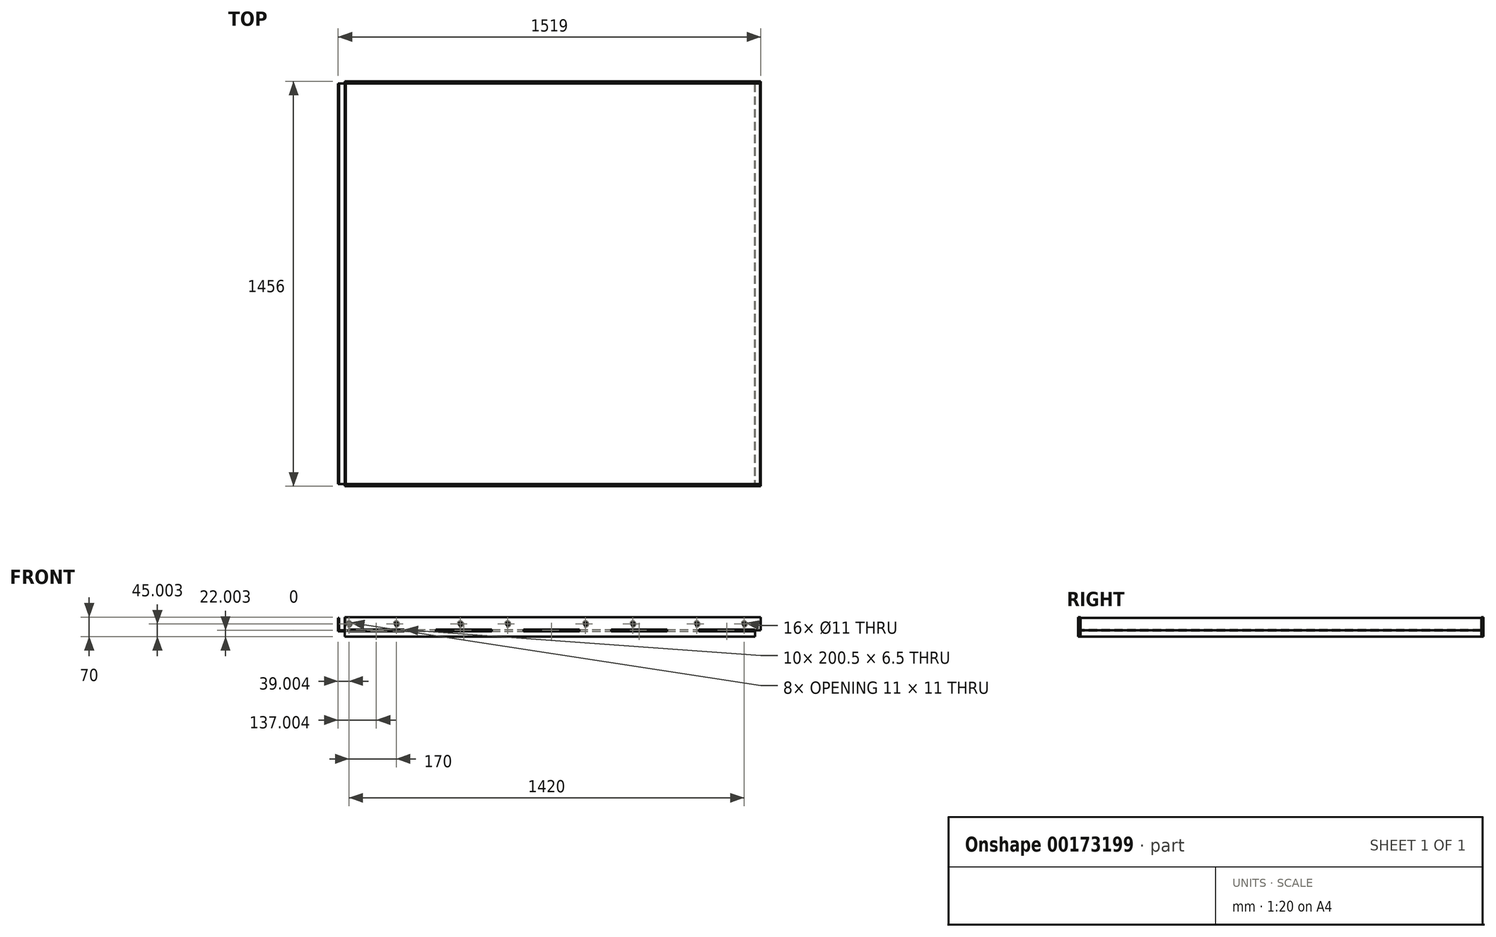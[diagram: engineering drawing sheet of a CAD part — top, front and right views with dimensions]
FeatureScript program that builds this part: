
annotation { "Feature Type Name" : "Feature", "Feature Type Description" : "" }
export const myFeature = defineFeature(function(context is Context, id is Id, definition is map)
    precondition{}
    {
        {
            var Q0;
            Q0=qCreatedBy(makeId("Front.planeOp"),FACE);
            var sketch = newSketch(context, id + "F0", { "sketchPlane" : qUnion([Q0])});
            skLineSegment(sketch, "E0", {"start": v(-1403.49, 88.26) * mm, "end": v(-1403.49, 40.26) * mm});
            skLineSegment(sketch, "E1", {"start": v(-1403.49, 40.26) * mm, "end": v(91.51, 40.26) * mm});
            skLineSegment(sketch, "E2", {"start": v(91.51, 40.26) * mm, "end": v(91.51, 21.26) * mm});
            skLineSegment(sketch, "E3", {"start": v(91.51, 21.26) * mm, "end": v(94.51, 21.26) * mm});
            skLineSegment(sketch, "E4", {"start": v(94.51, 21.26) * mm, "end": v(94.51, 43.26) * mm});
            skLineSegment(sketch, "E5", {"start": v(94.51, 43.26) * mm, "end": v(-1400.49, 43.26) * mm});
            skLineSegment(sketch, "E6", {"start": v(-1400.49, 43.26) * mm, "end": v(-1400.49, 88.26) * mm});
            skLineSegment(sketch, "E7", {"start": v(-1400.49, 88.26) * mm, "end": v(-1403.49, 88.26) * mm});
            skLineSegment(sketch, "E8", {"start": v(-1379.49, 43.26) * mm, "end": v(-1379.49, 88.26) * mm});
            skLineSegment(sketch, "E9", {"start": v(-1379.49, 88.26) * mm, "end": v(-1376.49, 88.26) * mm});
            skLineSegment(sketch, "E10", {"start": v(-1376.49, 88.26) * mm, "end": v(-1376.49, 46.26) * mm});
            skLineSegment(sketch, "E11", {"start": v(-1376.49, 46.26) * mm, "end": v(112.51, 46.26) * mm});
            skLineSegment(sketch, "E12", {"start": v(115.51, 46.26) * mm, "end": v(115.51, 43.26) * mm});
            skLineSegment(sketch, "E13", {"start": v(-1379.49, 43.26) * mm, "end": v(115.51, 43.26) * mm});
            skLineSegment(sketch, "E14", {"start": v(115.51, 46.26) * mm, "end": v(115.51, 88.26) * mm});
            skLineSegment(sketch, "E15", {"start": v(115.51, 88.26) * mm, "end": v(112.51, 88.26) * mm});
            skLineSegment(sketch, "E16", {"start": v(112.51, 88.26) * mm, "end": v(112.51, 46.26) * mm});
            skLineSegment(sketch, "E17.bottom", {"start": v(-1397.49, 82.67) * mm, "end": v(-1382.49, 82.67) * mm, "construction": true});
            skLineSegment(sketch, "E17.top", {"start": v(-1397.49, 47.75) * mm, "end": v(-1382.49, 47.75) * mm, "construction": true});
            skLineSegment(sketch, "E17.left", {"start": v(-1397.49, 82.67) * mm, "end": v(-1397.49, 47.75) * mm, "construction": true});
            skLineSegment(sketch, "E17.right", {"start": v(-1382.49, 82.67) * mm, "end": v(-1382.49, 47.75) * mm, "construction": true});
            skSolve(sketch);
        }
        {
            var Q0;
            Q0=makeQuery(id+"F0.imprint","IMPRINT",FACE,{"disambiguationData":[TD([[makeQuery(id+"F0.imprint","IMPRINT",EDGE,{"derivedFrom":sQuery(id+"F0.wireOp",EDGE,"E0")}),1.0]])]});
            extrude(context, id + "F1", {"entities" : qUnion([Q0]), "oppositeDirection" : true, "depth" : 1440 * mm});
        }
        {
            var Q0;
            {var subQ0=sQuery(id+"F0.wireOp",EDGE,"E8");Q0=makeQuery(id+"F0.imprint","IMPRINT",FACE,{"disambiguationData":[TD([[makeQuery(id+"F0.imprint","IMPRINT",EDGE,{"derivedFrom":subQ0}),-1.0]])]});}
            extrude(context, id + "F2", {"entities" : qUnion([Q0]), "oppositeDirection" : true, "depth" : 1440 * mm});
        }
        {
            var Q0;
            Q0=makeQuery(id+"F1.opExtrude","SWEPT_FACE",FACE,{"disambiguationData":[OSD([sQuery(id+"F0.wireOp",EDGE,"E5"),sQuery(id+"F0.wireOp",EDGE,"E13")])]});
            var sketch = newSketch(context, id + "F3", { "sketchPlane" : qUnion([Q0])});
            skLineSegment(sketch, "E18.bottom", {"start": v(-1366.49, 0) * mm, "end": v(-1166.49, 0) * mm});
            skLineSegment(sketch, "E18.top", {"start": v(-1366.49, -7) * mm, "end": v(-1166.49, -7) * mm});
            skLineSegment(sketch, "E18.left", {"start": v(-1366.49, 0) * mm, "end": v(-1366.49, -7) * mm});
            skLineSegment(sketch, "E18.right", {"start": v(-1166.49, 0) * mm, "end": v(-1166.49, -7) * mm});
            skLineSegment(sketch, "E19.1.0.0", {"start": v(-1051.49, 0) * mm, "end": v(-851.49, 0) * mm});
            skLineSegment(sketch, "E19.1.0.1", {"start": v(-1051.49, -7) * mm, "end": v(-851.49, -7) * mm});
            skLineSegment(sketch, "E19.1.0.2", {"start": v(-851.49, 0) * mm, "end": v(-851.49, -7) * mm});
            skLineSegment(sketch, "E19.1.0.3", {"start": v(-1051.49, 0) * mm, "end": v(-1051.49, -7) * mm});
            skLineSegment(sketch, "E19.2.0.0", {"start": v(-736.49, 0) * mm, "end": v(-536.49, 0) * mm});
            skLineSegment(sketch, "E19.2.0.1", {"start": v(-736.49, -7) * mm, "end": v(-536.49, -7) * mm});
            skLineSegment(sketch, "E19.2.0.2", {"start": v(-536.49, 0) * mm, "end": v(-536.49, -7) * mm});
            skLineSegment(sketch, "E19.2.0.3", {"start": v(-736.49, 0) * mm, "end": v(-736.49, -7) * mm});
            skLineSegment(sketch, "E19.3.0.0", {"start": v(-421.49, 0) * mm, "end": v(-221.49, 0) * mm});
            skLineSegment(sketch, "E19.3.0.1", {"start": v(-421.49, -7) * mm, "end": v(-221.49, -7) * mm});
            skLineSegment(sketch, "E19.3.0.2", {"start": v(-221.49, 0) * mm, "end": v(-221.49, -7) * mm});
            skLineSegment(sketch, "E19.3.0.3", {"start": v(-421.49, 0) * mm, "end": v(-421.49, -7) * mm});
            skLineSegment(sketch, "E19.4.0.0", {"start": v(-106.49, 0) * mm, "end": v(93.51, 0) * mm});
            skLineSegment(sketch, "E19.4.0.1", {"start": v(-106.49, -7) * mm, "end": v(93.51, -7) * mm});
            skLineSegment(sketch, "E19.4.0.2", {"start": v(93.51, 0) * mm, "end": v(93.51, -7) * mm});
            skLineSegment(sketch, "E19.4.0.3", {"start": v(-106.49, 0) * mm, "end": v(-106.49, -7) * mm});
            skLineSegment(sketch, "E19.direction1", {"start": v(-1366.49, -7) * mm, "end": v(-1051.49, -7) * mm, "construction": true});
            skLineSegment(sketch, "E20", {"start": v(-1400.49, 720) * mm, "end": v(412.72, 720) * mm, "construction": true});
            skLineSegment(sketch, "E21.MirrorCS", {"start": v(-1366.49, 1440) * mm, "end": v(-1366.49, 1447) * mm});
            skLineSegment(sketch, "E22.MirrorCS", {"start": v(-1051.49, 1440) * mm, "end": v(-1051.49, 1447) * mm});
            skLineSegment(sketch, "E23.MirrorCS", {"start": v(-421.49, 1440) * mm, "end": v(-421.49, 1447) * mm});
            skLineSegment(sketch, "E24.MirrorCS", {"start": v(93.51, 1440) * mm, "end": v(93.51, 1447) * mm});
            skLineSegment(sketch, "E25.MirrorCS", {"start": v(-221.49, 1440) * mm, "end": v(-221.49, 1447) * mm});
            skLineSegment(sketch, "E26.MirrorCS", {"start": v(-106.49, 1440) * mm, "end": v(-106.49, 1447) * mm});
            skLineSegment(sketch, "E27.MirrorCS", {"start": v(-736.49, 1440) * mm, "end": v(-736.49, 1447) * mm});
            skLineSegment(sketch, "E28.MirrorCS", {"start": v(-536.49, 1440) * mm, "end": v(-536.49, 1447) * mm});
            skLineSegment(sketch, "E29.MirrorCS", {"start": v(-851.49, 1440) * mm, "end": v(-851.49, 1447) * mm});
            skLineSegment(sketch, "E30.MirrorCS", {"start": v(-1166.49, 1440) * mm, "end": v(-1166.49, 1447) * mm});
            skLineSegment(sketch, "E31.MirrorCS", {"start": v(-1366.49, 1440) * mm, "end": v(-1166.49, 1440) * mm});
            skLineSegment(sketch, "E32.MirrorCS", {"start": v(-106.49, 1447) * mm, "end": v(93.51, 1447) * mm});
            skLineSegment(sketch, "E33.MirrorCS", {"start": v(-421.49, 1440) * mm, "end": v(-221.49, 1440) * mm});
            skLineSegment(sketch, "E34.MirrorCS", {"start": v(-736.49, 1440) * mm, "end": v(-536.49, 1440) * mm});
            skLineSegment(sketch, "E35.MirrorCS", {"start": v(-1366.49, 1447) * mm, "end": v(-1166.49, 1447) * mm});
            skLineSegment(sketch, "E36.MirrorCS", {"start": v(-1051.49, 1440) * mm, "end": v(-851.49, 1440) * mm});
            skLineSegment(sketch, "E37.MirrorCS", {"start": v(-106.49, 1440) * mm, "end": v(93.51, 1440) * mm});
            skLineSegment(sketch, "E38.MirrorCS", {"start": v(-421.49, 1447) * mm, "end": v(-221.49, 1447) * mm});
            skLineSegment(sketch, "E39.MirrorCS", {"start": v(-1366.49, 1447) * mm, "end": v(-1051.49, 1447) * mm, "construction": true});
            skLineSegment(sketch, "E40.MirrorCS", {"start": v(-736.49, 1447) * mm, "end": v(-536.49, 1447) * mm});
            skLineSegment(sketch, "E41.MirrorCS", {"start": v(-1051.49, 1447) * mm, "end": v(-851.49, 1447) * mm});
            skSolve(sketch);
        }
        {
            var Q0;
            Q0 = qSketchRegion(id + "F3", true);
            extrude(context, id + "F4", {"entities" : qUnion([Q0]), "operationType" : NewBodyOperationType.ADD, "oppositeDirection" : true, "depth" : 3 * mm});
        }
        {
            var Q0;
            Q0=makeQuery(id+"F2.opExtrude","SWEPT_FACE",FACE,{"disambiguationData":[OSD([sQuery(id+"F0.wireOp",EDGE,"E11")])]});
            var sketch = newSketch(context, id + "F5", { "sketchPlane" : qUnion([Q0])});
            skLineSegment(sketch, "E42.bottom", {"start": v(-1366.49, 0) * mm, "end": v(-1166.49, 0) * mm});
            skLineSegment(sketch, "E42.top", {"start": v(-1366.49, -7) * mm, "end": v(-1166.49, -7) * mm});
            skLineSegment(sketch, "E42.left", {"start": v(-1366.49, 0) * mm, "end": v(-1366.49, -7) * mm});
            skLineSegment(sketch, "E42.right", {"start": v(-1166.49, 0) * mm, "end": v(-1166.49, -7) * mm});
            skLineSegment(sketch, "E43.1.0.0", {"start": v(-1051.49, -7) * mm, "end": v(-851.49, -7) * mm});
            skLineSegment(sketch, "E43.1.0.1", {"start": v(-1051.49, 0) * mm, "end": v(-851.49, 0) * mm});
            skLineSegment(sketch, "E43.1.0.2", {"start": v(-1051.49, 0) * mm, "end": v(-1051.49, -7) * mm});
            skLineSegment(sketch, "E43.1.0.3", {"start": v(-851.49, 0) * mm, "end": v(-851.49, -7) * mm});
            skLineSegment(sketch, "E43.2.0.0", {"start": v(-736.49, -7) * mm, "end": v(-536.49, -7) * mm});
            skLineSegment(sketch, "E43.2.0.1", {"start": v(-736.49, 0) * mm, "end": v(-536.49, 0) * mm});
            skLineSegment(sketch, "E43.2.0.2", {"start": v(-736.49, 0) * mm, "end": v(-736.49, -7) * mm});
            skLineSegment(sketch, "E43.2.0.3", {"start": v(-536.49, 0) * mm, "end": v(-536.49, -7) * mm});
            skLineSegment(sketch, "E43.3.0.0", {"start": v(-421.49, -7) * mm, "end": v(-221.49, -7) * mm});
            skLineSegment(sketch, "E43.3.0.1", {"start": v(-421.49, 0) * mm, "end": v(-221.49, 0) * mm});
            skLineSegment(sketch, "E43.3.0.2", {"start": v(-421.49, 0) * mm, "end": v(-421.49, -7) * mm});
            skLineSegment(sketch, "E43.3.0.3", {"start": v(-221.49, 0) * mm, "end": v(-221.49, -7) * mm});
            skLineSegment(sketch, "E43.4.0.0", {"start": v(-106.49, -7) * mm, "end": v(93.51, -7) * mm});
            skLineSegment(sketch, "E43.4.0.1", {"start": v(-106.49, 0) * mm, "end": v(93.51, 0) * mm});
            skLineSegment(sketch, "E43.4.0.2", {"start": v(-106.49, 0) * mm, "end": v(-106.49, -7) * mm});
            skLineSegment(sketch, "E43.4.0.3", {"start": v(93.51, 0) * mm, "end": v(93.51, -7) * mm});
            skLineSegment(sketch, "E43.direction1", {"start": v(-1366.49, -7) * mm, "end": v(-1051.49, -7) * mm, "construction": true});
            skLineSegment(sketch, "E44", {"start": v(-1376.49, 720) * mm, "end": v(410.62, 720) * mm, "construction": true});
            skPoint(sketch, "E44.endSnap0", {"position": v(112.51, 720) * mm});
            skLineSegment(sketch, "E45.MirrorCS", {"start": v(-1051.49, 1440) * mm, "end": v(-1051.49, 1447) * mm});
            skLineSegment(sketch, "E46.MirrorCS", {"start": v(-1366.49, 1440) * mm, "end": v(-1366.49, 1447) * mm});
            skLineSegment(sketch, "E47.MirrorCS", {"start": v(-106.49, 1440) * mm, "end": v(-106.49, 1447) * mm});
            skLineSegment(sketch, "E48.MirrorCS", {"start": v(-536.49, 1440) * mm, "end": v(-536.49, 1447) * mm});
            skLineSegment(sketch, "E49.MirrorCS", {"start": v(-736.49, 1440) * mm, "end": v(-736.49, 1447) * mm});
            skLineSegment(sketch, "E50.MirrorCS", {"start": v(-851.49, 1440) * mm, "end": v(-851.49, 1447) * mm});
            skLineSegment(sketch, "E51.MirrorCS", {"start": v(-1166.49, 1440) * mm, "end": v(-1166.49, 1447) * mm});
            skLineSegment(sketch, "E52.MirrorCS", {"start": v(93.51, 1440) * mm, "end": v(93.51, 1447) * mm});
            skLineSegment(sketch, "E53.MirrorCS", {"start": v(-221.49, 1440) * mm, "end": v(-221.49, 1447) * mm});
            skLineSegment(sketch, "E54.MirrorCS", {"start": v(-421.49, 1440) * mm, "end": v(-421.49, 1447) * mm});
            skLineSegment(sketch, "E55.MirrorCS", {"start": v(-1366.49, 1447) * mm, "end": v(-1166.49, 1447) * mm});
            skLineSegment(sketch, "E56.MirrorCS", {"start": v(-1366.49, 1447) * mm, "end": v(-1051.49, 1447) * mm, "construction": true});
            skLineSegment(sketch, "E57.MirrorCS", {"start": v(-106.49, 1447) * mm, "end": v(93.51, 1447) * mm});
            skLineSegment(sketch, "E58.MirrorCS", {"start": v(-421.49, 1447) * mm, "end": v(-221.49, 1447) * mm});
            skLineSegment(sketch, "E59.MirrorCS", {"start": v(-736.49, 1440) * mm, "end": v(-536.49, 1440) * mm});
            skLineSegment(sketch, "E60.MirrorCS", {"start": v(-736.49, 1447) * mm, "end": v(-536.49, 1447) * mm});
            skLineSegment(sketch, "E61.MirrorCS", {"start": v(-1051.49, 1440) * mm, "end": v(-851.49, 1440) * mm});
            skLineSegment(sketch, "E62.MirrorCS", {"start": v(-1051.49, 1447) * mm, "end": v(-851.49, 1447) * mm});
            skLineSegment(sketch, "E63.MirrorCS", {"start": v(-1366.49, 1440) * mm, "end": v(-1166.49, 1440) * mm});
            skLineSegment(sketch, "E64.MirrorCS", {"start": v(-106.49, 1440) * mm, "end": v(93.51, 1440) * mm});
            skLineSegment(sketch, "E65.MirrorCS", {"start": v(-421.49, 1440) * mm, "end": v(-221.49, 1440) * mm});
            skSolve(sketch);
        }
        {
            var Q0;
            Q0 = qSketchRegion(id + "F5", true);
            extrude(context, id + "F6", {"entities" : qUnion([Q0]), "operationType" : NewBodyOperationType.ADD, "oppositeDirection" : true, "depth" : 3 * mm});
        }
        {
            var Q0;
            {var subQ20=sQuery(id+"F0.wireOp",EDGE,"E1");var subQ29=sQuery(id+"F0.wireOp",EDGE,"E6");var subQ34=sQuery(id+"F0.wireOp",EDGE,"E0");var subQ35=sQuery(id+"F0.wireOp",EDGE,"E7");var subQ40=sQuery(id+"F0.wireOp",EDGE,"E13");var subQ41=sQuery(id+"F0.wireOp",EDGE,"E5");Q0=makeQuery(id+"F4.boolean.opBoolean","SPLIT",FACE,{"disambiguationData":[TD([makeQuery(id+"F1.opExtrude","SWEPT_FACE",FACE,{"disambiguationData":[OSD([subQ34])]})])],"derivedFrom":makeQuery(id+"F1.opExtrude","CAP_FACE",FACE,{"disambiguationData":[OSD([subQ34,subQ20,sQuery(id+"F0.wireOp",EDGE,"E2"),sQuery(id+"F0.wireOp",EDGE,"E3"),sQuery(id+"F0.wireOp",EDGE,"E4"),subQ41,subQ29,subQ35,subQ40])],"isStart":true})});}
            var sketch = newSketch(context, id + "F7", { "sketchPlane" : qUnion([Q0])});
            skLineSegment(sketch, "E66", {"start": v(115.51, 43.26) * mm, "end": v(94.51, 43.26) * mm});
            skLineSegment(sketch, "E67", {"start": v(94.51, 43.26) * mm, "end": v(94.51, 21.26) * mm});
            skLineSegment(sketch, "E68", {"start": v(94.51, 21.26) * mm, "end": v(-1379.49, 21.26) * mm});
            skLineSegment(sketch, "E69", {"start": v(-1379.49, 21.26) * mm, "end": v(-1379.49, 91.26) * mm});
            skLineSegment(sketch, "E70", {"start": v(-1379.49, 91.26) * mm, "end": v(115.51, 91.26) * mm});
            skLineSegment(sketch, "E71", {"start": v(115.51, 91.26) * mm, "end": v(115.51, 43.26) * mm});
            skLineSegment(sketch, "E72.bottom", {"start": v(-1366.74, 46.51) * mm, "end": v(-1166.24, 46.51) * mm});
            skLineSegment(sketch, "E72.top", {"start": v(-1366.74, 40.01) * mm, "end": v(-1166.24, 40.01) * mm});
            skLineSegment(sketch, "E72.left", {"start": v(-1366.74, 46.51) * mm, "end": v(-1366.74, 40.01) * mm});
            skLineSegment(sketch, "E72.right", {"start": v(-1166.24, 46.51) * mm, "end": v(-1166.24, 40.01) * mm});
            skLineSegment(sketch, "E73.1.0.0", {"start": v(-1051.74, 46.51) * mm, "end": v(-851.24, 46.51) * mm});
            skLineSegment(sketch, "E73.1.0.1", {"start": v(-1051.74, 40.01) * mm, "end": v(-851.24, 40.01) * mm});
            skLineSegment(sketch, "E73.1.0.2", {"start": v(-1051.74, 46.51) * mm, "end": v(-1051.74, 40.01) * mm});
            skLineSegment(sketch, "E73.1.0.3", {"start": v(-851.24, 46.51) * mm, "end": v(-851.24, 40.01) * mm});
            skLineSegment(sketch, "E73.2.0.0", {"start": v(-736.74, 46.51) * mm, "end": v(-536.24, 46.51) * mm});
            skLineSegment(sketch, "E73.2.0.1", {"start": v(-736.74, 40.01) * mm, "end": v(-536.24, 40.01) * mm});
            skLineSegment(sketch, "E73.2.0.2", {"start": v(-736.74, 46.51) * mm, "end": v(-736.74, 40.01) * mm});
            skLineSegment(sketch, "E73.2.0.3", {"start": v(-536.24, 46.51) * mm, "end": v(-536.24, 40.01) * mm});
            skLineSegment(sketch, "E73.3.0.0", {"start": v(-421.74, 46.51) * mm, "end": v(-221.24, 46.51) * mm});
            skLineSegment(sketch, "E73.3.0.1", {"start": v(-421.74, 40.01) * mm, "end": v(-221.24, 40.01) * mm});
            skLineSegment(sketch, "E73.3.0.2", {"start": v(-421.74, 46.51) * mm, "end": v(-421.74, 40.01) * mm});
            skLineSegment(sketch, "E73.3.0.3", {"start": v(-221.24, 46.51) * mm, "end": v(-221.24, 40.01) * mm});
            skLineSegment(sketch, "E73.4.0.0", {"start": v(-106.74, 46.51) * mm, "end": v(93.76, 46.51) * mm});
            skLineSegment(sketch, "E73.4.0.1", {"start": v(-106.74, 40.01) * mm, "end": v(93.76, 40.01) * mm});
            skLineSegment(sketch, "E73.4.0.2", {"start": v(-106.74, 46.51) * mm, "end": v(-106.74, 40.01) * mm});
            skLineSegment(sketch, "E73.4.0.3", {"start": v(93.76, 46.51) * mm, "end": v(93.76, 40.01) * mm});
            skLineSegment(sketch, "E73.direction1", {"start": v(-1366.74, 40.01) * mm, "end": v(-1051.74, 40.01) * mm, "construction": true});
            skSolve(sketch);
        }
        {
            var Q0;
            Q0 = qSketchRegion(id + "F7", true);
            extrude(context, id + "F8", {"entities" : qUnion([Q0]), "depth" : 8 * mm});
        }
        {
            var Q0;
            Q0=sQuery(id+"F5.wireOp",EDGE,"E44");
            cPlane(context, id + "F9", {"entities" : qUnion([Q0]), "cplaneType" : CPlaneType.LINE_ANGLE, "offset" : 25 * mm, "angle" : 0 * degree, "width" : 150 * mm, "height" : 150 * mm});
        }
        {
            var Q0;
            Q0=makeQuery(id+"F8.opExtrude","CAP_FACE",FACE,{"disambiguationData":[OSD([sQuery(id+"F7.wireOp",EDGE,"E66"),sQuery(id+"F7.wireOp",EDGE,"E67"),sQuery(id+"F7.wireOp",EDGE,"E68"),sQuery(id+"F7.wireOp",EDGE,"E69"),sQuery(id+"F7.wireOp",EDGE,"E70"),sQuery(id+"F7.wireOp",EDGE,"E71"),sQuery(id+"F7.wireOp",EDGE,"E72.bottom"),sQuery(id+"F7.wireOp",EDGE,"E72.top"),sQuery(id+"F7.wireOp",EDGE,"E72.left"),sQuery(id+"F7.wireOp",EDGE,"E72.right"),sQuery(id+"F7.wireOp",EDGE,"E73.1.0.0"),sQuery(id+"F7.wireOp",EDGE,"E73.1.0.1"),sQuery(id+"F7.wireOp",EDGE,"E73.1.0.2"),sQuery(id+"F7.wireOp",EDGE,"E73.1.0.3"),sQuery(id+"F7.wireOp",EDGE,"E73.2.0.0"),sQuery(id+"F7.wireOp",EDGE,"E73.2.0.1"),sQuery(id+"F7.wireOp",EDGE,"E73.2.0.2"),sQuery(id+"F7.wireOp",EDGE,"E73.2.0.3"),sQuery(id+"F7.wireOp",EDGE,"E73.3.0.0"),sQuery(id+"F7.wireOp",EDGE,"E73.3.0.1"),sQuery(id+"F7.wireOp",EDGE,"E73.3.0.2"),sQuery(id+"F7.wireOp",EDGE,"E73.3.0.3"),sQuery(id+"F7.wireOp",EDGE,"E73.4.0.0"),sQuery(id+"F7.wireOp",EDGE,"E73.4.0.1"),sQuery(id+"F7.wireOp",EDGE,"E73.4.0.2"),sQuery(id+"F7.wireOp",EDGE,"E73.4.0.3")])],"isStart":true});
            var sketch = newSketch(context, id + "F10", { "sketchPlane" : qUnion([Q0])});
            skPoint(sketch, "E74", {"position": v(-55.51, 66.26) * mm});
            skPoint(sketch, "E75", {"position": v(114.49, 66.26) * mm});
            skPoint(sketch, "E76", {"position": v(344.49, 66.26) * mm});
            skPoint(sketch, "E77", {"position": v(514.49, 66.26) * mm});
            skPoint(sketch, "E78", {"position": v(794.49, 66.26) * mm});
            skPoint(sketch, "E79", {"position": v(964.49, 66.26) * mm});
            skPoint(sketch, "E80", {"position": v(1194.49, 66.26) * mm});
            skPoint(sketch, "E81", {"position": v(1364.49, 66.26) * mm});
            skSolve(sketch);
        }
        {
            var Q0;
            Q0=sQuery(id+"F10.wireOp",VERTEX,"E81");
            var Q1;
            Q1=sQuery(id+"F10.wireOp",VERTEX,"E80");
            var Q2;
            Q2=sQuery(id+"F10.wireOp",VERTEX,"E79");
            var Q3;
            Q3=sQuery(id+"F10.wireOp",VERTEX,"E78");
            var Q4;
            Q4=sQuery(id+"F10.wireOp",VERTEX,"E77");
            var Q5;
            Q5=sQuery(id+"F10.wireOp",VERTEX,"E76");
            var Q6;
            Q6=sQuery(id+"F10.wireOp",VERTEX,"E75");
            var Q7;
            Q7=sQuery(id+"F10.wireOp",VERTEX,"E74");
            var Q8;
            Q8=makeQuery(id+"F8.opExtrude","SWEPT_BODY",BODY,{"disambiguationData":[OSD([sQuery(id+"F7.wireOp",EDGE,"E66"),sQuery(id+"F7.wireOp",EDGE,"E67"),sQuery(id+"F7.wireOp",EDGE,"E68"),sQuery(id+"F7.wireOp",EDGE,"E69"),sQuery(id+"F7.wireOp",EDGE,"E70"),sQuery(id+"F7.wireOp",EDGE,"E71"),sQuery(id+"F7.wireOp",EDGE,"E72.bottom"),sQuery(id+"F7.wireOp",EDGE,"E72.top"),sQuery(id+"F7.wireOp",EDGE,"E72.left"),sQuery(id+"F7.wireOp",EDGE,"E72.right"),sQuery(id+"F7.wireOp",EDGE,"E73.1.0.0"),sQuery(id+"F7.wireOp",EDGE,"E73.1.0.1"),sQuery(id+"F7.wireOp",EDGE,"E73.1.0.2"),sQuery(id+"F7.wireOp",EDGE,"E73.1.0.3"),sQuery(id+"F7.wireOp",EDGE,"E73.2.0.0"),sQuery(id+"F7.wireOp",EDGE,"E73.2.0.1"),sQuery(id+"F7.wireOp",EDGE,"E73.2.0.2"),sQuery(id+"F7.wireOp",EDGE,"E73.2.0.3"),sQuery(id+"F7.wireOp",EDGE,"E73.3.0.0"),sQuery(id+"F7.wireOp",EDGE,"E73.3.0.1"),sQuery(id+"F7.wireOp",EDGE,"E73.3.0.2"),sQuery(id+"F7.wireOp",EDGE,"E73.3.0.3"),sQuery(id+"F7.wireOp",EDGE,"E73.4.0.0"),sQuery(id+"F7.wireOp",EDGE,"E73.4.0.1"),sQuery(id+"F7.wireOp",EDGE,"E73.4.0.2"),sQuery(id+"F7.wireOp",EDGE,"E73.4.0.3")])]});
            hole(context, id + "F11", {"style" : HoleStyle.C_SINK, "endStyle" : HoleEndStyle.THROUGH, "holeDiameter" : 11 * mm, "cSinkDiameter" : 22 * mm, "cSinkAngle" : 90 * degree, "locations" : qUnion([Q0, Q1, Q2, Q3, Q4, Q5, Q6, Q7]), "scope" : qUnion([Q8]), "isTappedThrough" : true});
        }
        {
            var Q0;
            Q0=makeQuery(id+"F8.opExtrude","SWEPT_BODY",BODY,{"disambiguationData":[OSD([sQuery(id+"F7.wireOp",EDGE,"E66"),sQuery(id+"F7.wireOp",EDGE,"E67"),sQuery(id+"F7.wireOp",EDGE,"E68"),sQuery(id+"F7.wireOp",EDGE,"E69"),sQuery(id+"F7.wireOp",EDGE,"E70"),sQuery(id+"F7.wireOp",EDGE,"E71"),sQuery(id+"F7.wireOp",EDGE,"E72.bottom"),sQuery(id+"F7.wireOp",EDGE,"E72.top"),sQuery(id+"F7.wireOp",EDGE,"E72.left"),sQuery(id+"F7.wireOp",EDGE,"E72.right"),sQuery(id+"F7.wireOp",EDGE,"E73.1.0.0"),sQuery(id+"F7.wireOp",EDGE,"E73.1.0.1"),sQuery(id+"F7.wireOp",EDGE,"E73.1.0.2"),sQuery(id+"F7.wireOp",EDGE,"E73.1.0.3"),sQuery(id+"F7.wireOp",EDGE,"E73.2.0.0"),sQuery(id+"F7.wireOp",EDGE,"E73.2.0.1"),sQuery(id+"F7.wireOp",EDGE,"E73.2.0.2"),sQuery(id+"F7.wireOp",EDGE,"E73.2.0.3"),sQuery(id+"F7.wireOp",EDGE,"E73.3.0.0"),sQuery(id+"F7.wireOp",EDGE,"E73.3.0.1"),sQuery(id+"F7.wireOp",EDGE,"E73.3.0.2"),sQuery(id+"F7.wireOp",EDGE,"E73.3.0.3"),sQuery(id+"F7.wireOp",EDGE,"E73.4.0.0"),sQuery(id+"F7.wireOp",EDGE,"E73.4.0.1"),sQuery(id+"F7.wireOp",EDGE,"E73.4.0.2"),sQuery(id+"F7.wireOp",EDGE,"E73.4.0.3")])]});
            var Q1;
            Q1=qCreatedBy(id+"F9.planeOp",FACE);
            mirror(context, id + "F12", {"entities" : qUnion([Q0]), "mirrorPlane" : qUnion([Q1])});
        }
    });
